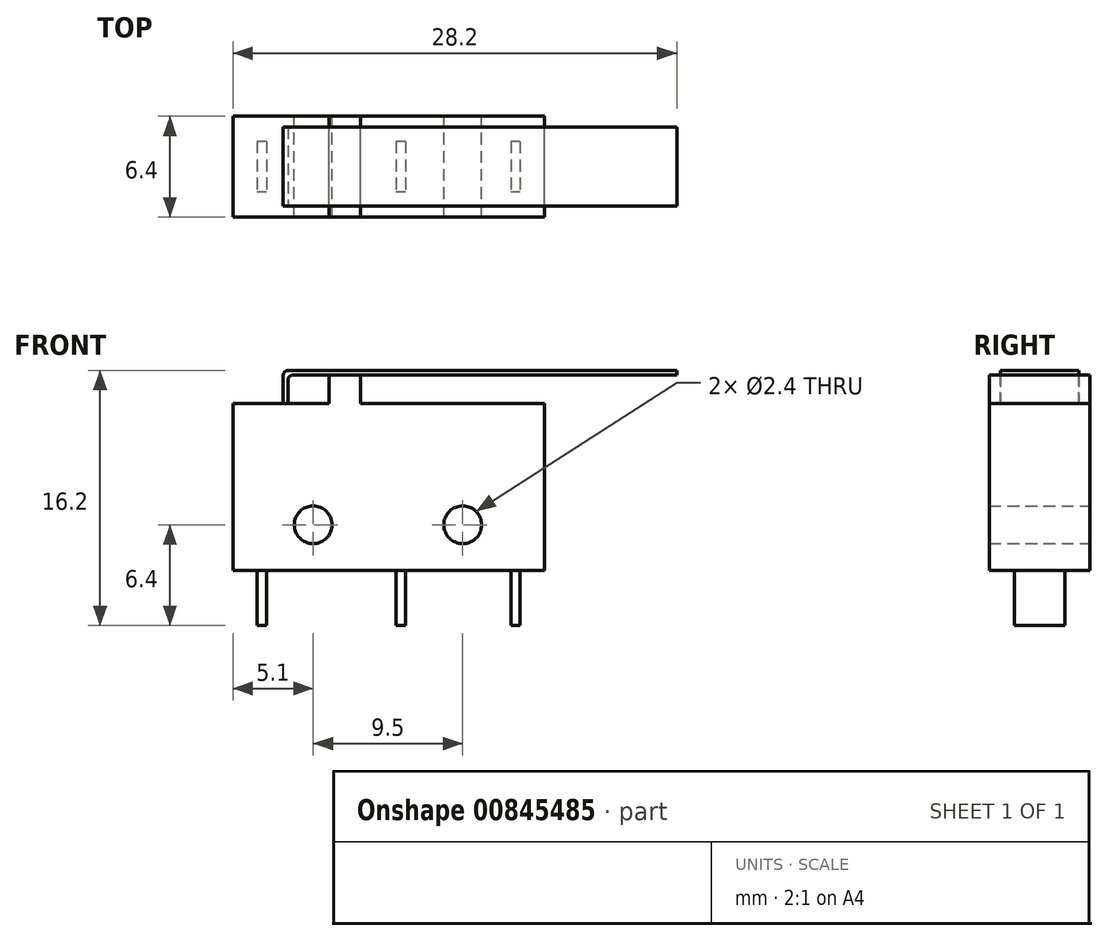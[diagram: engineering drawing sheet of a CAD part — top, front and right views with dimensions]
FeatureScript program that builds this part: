
annotation { "Feature Type Name" : "Feature", "Feature Type Description" : "" }
export const myFeature = defineFeature(function(context is Context, id is Id, definition is map)
    precondition{}
    {
        {
            var Q0;
            Q0=qCreatedBy(makeId("Front.planeOp"),FACE);
            var sketch = newSketch(context, id + "F0", { "sketchPlane" : qUnion([Q0])});
            skLineSegment(sketch, "E0.bottom", {"start": v(0, 0) * mm, "end": v(19.8, 0) * mm});
            skLineSegment(sketch, "E0.top", {"start": v(0, 10.6) * mm, "end": v(6.1, 10.6) * mm});
            skLineSegment(sketch, "E0.left", {"start": v(0, 0) * mm, "end": v(0, 10.6) * mm});
            skLineSegment(sketch, "E0.right", {"start": v(19.8, 0) * mm, "end": v(19.8, 10.6) * mm});
            skCircle(sketch, "E1", {"center": v(5.1, 2.9) * mm, "radius": 1.2 * mm});
            skCircle(sketch, "E2", {"center": v(14.6, 2.9) * mm, "radius": 1.2 * mm});
            skLineSegment(sketch, "E3", {"start": v(6.1, 10.6) * mm, "end": v(6.1, 12.4) * mm});
            skLineSegment(sketch, "E4", {"start": v(6.1, 12.4) * mm, "end": v(8.1, 12.4) * mm});
            skLineSegment(sketch, "E5", {"start": v(8.1, 12.4) * mm, "end": v(8.1, 10.6) * mm});
            skLineSegment(sketch, "E6.trimOffspring", {"start": v(8.1, 10.6) * mm, "end": v(19.8, 10.6) * mm});
            skSolve(sketch);
        }
        {
            var Q0;
            Q0=qSketchRegion(id+"F0",true);
            extrude(context, id + "F1", {"entities" : qUnion([Q0]), "depth" : 6.4 * mm, "offsetDistance" : 25 * mm});
        }
        {
            var Q0;
            Q0=makeQuery(id+"F1.opExtrude","SWEPT_FACE",FACE,{"disambiguationData":[OSD([sQuery(id+"F0.wireOp",EDGE,"E0.bottom")])]});
            var sketch = newSketch(context, id + "F2", { "sketchPlane" : qUnion([Q0])});
            skLineSegment(sketch, "E7", {"start": v(0, 3.2) * mm, "end": v(19.8, 3.2) * mm, "construction": true});
            skLineSegment(sketch, "E8.bottom", {"start": v(2.15, 1.6) * mm, "end": v(1.55, 1.6) * mm});
            skLineSegment(sketch, "E8.top", {"start": v(2.15, 4.8) * mm, "end": v(1.55, 4.8) * mm});
            skLineSegment(sketch, "E8.left", {"start": v(2.15, 1.6) * mm, "end": v(2.15, 4.8) * mm});
            skLineSegment(sketch, "E8.right", {"start": v(1.55, 1.6) * mm, "end": v(1.55, 4.8) * mm});
            skPoint(sketch, "E8.middle", {"position": v(1.85, 3.2) * mm});
            skLineSegment(sketch, "E9.bottom", {"start": v(10.95, 1.6) * mm, "end": v(10.35, 1.6) * mm});
            skLineSegment(sketch, "E9.top", {"start": v(10.95, 4.8) * mm, "end": v(10.35, 4.8) * mm});
            skLineSegment(sketch, "E9.left", {"start": v(10.95, 1.6) * mm, "end": v(10.95, 4.8) * mm});
            skLineSegment(sketch, "E9.right", {"start": v(10.35, 1.6) * mm, "end": v(10.35, 4.8) * mm});
            skPoint(sketch, "E9.middle", {"position": v(10.65, 3.2) * mm});
            skLineSegment(sketch, "E10.bottom", {"start": v(18.25, 1.6) * mm, "end": v(17.65, 1.6) * mm});
            skLineSegment(sketch, "E10.top", {"start": v(18.25, 4.8) * mm, "end": v(17.65, 4.8) * mm});
            skLineSegment(sketch, "E10.left", {"start": v(18.25, 1.6) * mm, "end": v(18.25, 4.8) * mm});
            skLineSegment(sketch, "E10.right", {"start": v(17.65, 1.6) * mm, "end": v(17.65, 4.8) * mm});
            skPoint(sketch, "E10.middle", {"position": v(17.95, 3.2) * mm});
            skSolve(sketch);
        }
        {
            var Q0;
            Q0=qSketchRegion(id+"F2",true);
            extrude(context, id + "F3", {"entities" : qUnion([Q0]), "depth" : 3.5 * mm, "offsetDistance" : 25 * mm});
        }
        {
            var Q0;
            Q0=makeQuery(id+"F1.opExtrude","SWEPT_FACE",FACE,{"disambiguationData":[OSD([sQuery(id+"F0.wireOp",EDGE,"E4")])]});
            var sketch = newSketch(context, id + "F4", { "sketchPlane" : qUnion([Q0])});
            skLineSegment(sketch, "E11.bottom", {"start": v(3.2, -0.7) * mm, "end": v(28.2, -0.7) * mm});
            skLineSegment(sketch, "E11.top", {"start": v(3.2, -5.7) * mm, "end": v(28.2, -5.7) * mm});
            skLineSegment(sketch, "E11.left", {"start": v(3.2, -0.7) * mm, "end": v(3.2, -5.7) * mm});
            skLineSegment(sketch, "E11.right", {"start": v(28.2, -0.7) * mm, "end": v(28.2, -5.7) * mm});
            skSolve(sketch);
        }
        {
            var Q0;
            Q0=qSketchRegion(id+"F4",true);
            extrude(context, id + "F5", {"entities" : qUnion([Q0]), "depth" : 0.3 * mm, "offsetDistance" : 25 * mm});
        }
        {
            var Q0;
            Q0=makeQuery(id+"F5.opExtrude","CAP_FACE",FACE,{"disambiguationData":[OSD([sQuery(id+"F4.wireOp",EDGE,"E11.bottom"),sQuery(id+"F4.wireOp",EDGE,"E11.top"),sQuery(id+"F4.wireOp",EDGE,"E11.left"),sQuery(id+"F4.wireOp",EDGE,"E11.right")])],"isStart":false});
            var sketch = newSketch(context, id + "F6", { "sketchPlane" : qUnion([Q0])});
            skLineSegment(sketch, "E12.bottom", {"start": v(3.2, -0.7) * mm, "end": v(3.5, -0.7) * mm});
            skLineSegment(sketch, "E12.top", {"start": v(3.2, -5.7) * mm, "end": v(3.5, -5.7) * mm});
            skLineSegment(sketch, "E12.left", {"start": v(3.2, -0.7) * mm, "end": v(3.2, -5.7) * mm});
            skLineSegment(sketch, "E12.right", {"start": v(3.5, -0.7) * mm, "end": v(3.5, -5.7) * mm});
            skSolve(sketch);
        }
        {
            var Q0;
            Q0=qSketchRegion(id+"F6",true);
            extrude(context, id + "F7", {"entities" : qUnion([Q0]), "operationType" : NewBodyOperationType.ADD, "oppositeDirection" : true, "depth" : 3 * mm, "offsetDistance" : 25 * mm});
        }
        {
            var Q0;
            Q0=makeQuery(id+"F5.opExtrude","CAP_EDGE",EDGE,{"disambiguationData":[OSD([sQuery(id+"F4.wireOp",EDGE,"E11.left")])],"isStart":false});
            var Q1;
            Q1=makeQuery(id+"F7.boolean.opBoolean","INTERSECT",EDGE,{"derivedFrom":[makeQuery(id+"F5.opExtrude","CAP_FACE",FACE,{"disambiguationData":[OSD([sQuery(id+"F4.wireOp",EDGE,"E11.bottom"),sQuery(id+"F4.wireOp",EDGE,"E11.top"),sQuery(id+"F4.wireOp",EDGE,"E11.left"),sQuery(id+"F4.wireOp",EDGE,"E11.right")])],"isStart":true}),makeQuery(id+"F7.opExtrude","SWEPT_FACE",FACE,{"disambiguationData":[OSD([sQuery(id+"F6.wireOp",EDGE,"E12.right")])]})]});
            fillet(context, id + "F8", {"entities" : qUnion([Q0, Q1]), "radius" : 0.3 * mm, "tangentPropagation" : true, "allowEdgeOverflow" : false});
        }
    });
